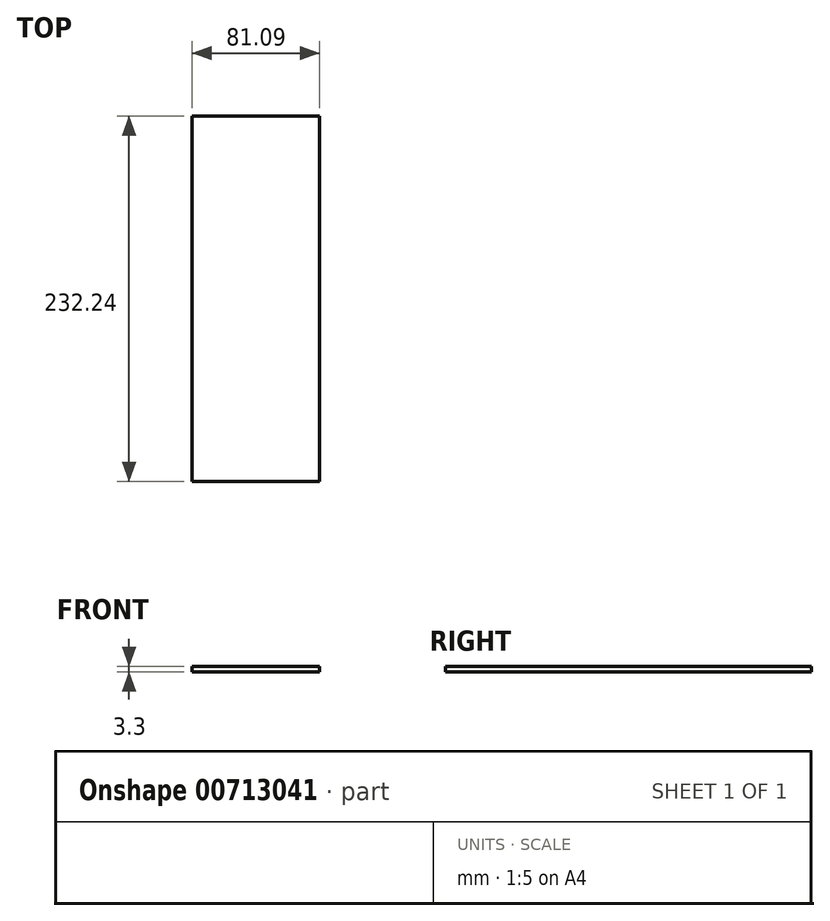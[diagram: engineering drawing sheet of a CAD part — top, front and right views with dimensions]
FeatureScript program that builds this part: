
annotation { "Feature Type Name" : "Feature", "Feature Type Description" : "" }
export const myFeature = defineFeature(function(context is Context, id is Id, definition is map)
    precondition{}
    {
        {
            var Q0;
            Q0=qCreatedBy(makeId("Top.planeOp"),FACE);
            var sketch = newSketch(context, id + "F0", { "sketchPlane" : qUnion([Q0])});
            skLineSegment(sketch, "E0.bottom", {"start": v(219.57, -232.24) * mm, "end": v(425.4, -232.24) * mm});
            skLineSegment(sketch, "E0.top", {"start": v(219.57, 106.84) * mm, "end": v(425.4, 106.84) * mm});
            skLineSegment(sketch, "E0.left", {"start": v(219.57, -232.24) * mm, "end": v(219.57, 106.84) * mm});
            skLineSegment(sketch, "E0.right", {"start": v(425.4, -232.24) * mm, "end": v(425.4, 106.84) * mm});
            skLineSegment(sketch, "E1.bottom", {"start": v(62.69, 0) * mm, "end": v(300.66, 0) * mm});
            skLineSegment(sketch, "E1.top", {"start": v(62.69, -468.2) * mm, "end": v(300.66, -468.2) * mm});
            skLineSegment(sketch, "E1.left", {"start": v(62.69, 0) * mm, "end": v(62.69, -468.2) * mm});
            skLineSegment(sketch, "E1.right", {"start": v(300.66, 0) * mm, "end": v(300.66, -468.2) * mm});
            skPoint(sketch, "E1.middle", {"position": v(181.67, -234.1) * mm});
            skLineSegment(sketch, "E2.bottom", {"start": v(464.3, -61.68) * mm, "end": v(324.9, -61.68) * mm});
            skLineSegment(sketch, "E2.top", {"start": v(464.3, 61.68) * mm, "end": v(324.9, 61.68) * mm});
            skLineSegment(sketch, "E2.left", {"start": v(464.3, -61.68) * mm, "end": v(464.3, 61.68) * mm});
            skLineSegment(sketch, "E2.right", {"start": v(324.9, -61.68) * mm, "end": v(324.9, 61.68) * mm});
            skPoint(sketch, "E2.middle", {"position": v(394.6, 0) * mm});
            skSolve(sketch);
        }
        {
            var Q0;
            Q0=makeQuery(id+"F0.imprint","IMPRINT",FACE,{"disambiguationData":[TD([[makeQuery(id+"F0.imprint","IMPRINT",EDGE,{"derivedFrom":sQuery(id+"F0.wireOp",EDGE,"E0.bottom")}),1.0]])]});
            extrude(context, id + "F1", {"entities" : qUnion([Q0]), "depth" : 3.3 * mm, "offsetDistance" : 25.4 * mm});
        }
    });
